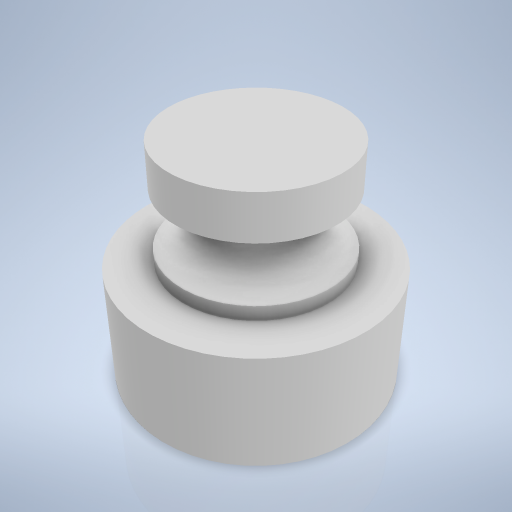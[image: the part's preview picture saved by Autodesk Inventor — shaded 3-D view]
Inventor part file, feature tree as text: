
AUTODESK INVENTOR PART (.ipt)
format: ipt  version: 2024.2 (Build 282272000, 272)  size: 270,336 bytes
history: native  units: mm
features: sketch x3, extrude x2, plane x1, revolve x1
ambient origin geometry x8: Origin, YZ Plane, XZ Plane, XY Plane, X Axis, Y Axis, Z Axis, Center Point
bodies: Volumenkörper1 (feature_tree)
feature tree (7):
  extrude  "Extrusion1"  Depth=20.0mm TaperAngle=0.0deg
  extrude  "Extrusion2"  Depth=20.0mm TaperAngle=0.0deg
  plane  "Arbeitsebene1"
  revolve  "Umdrehung1"
  sketch  "Skizze1"  dims[d0=45.0mm d1=20.0mm d2=0.0mm]
  sketch  "Skizze3"  dims[d3=30.0mm d4=20.0mm d5=0.0mm]
  sketch  "Skizze5"  dims[d6=0.0mm d8=20.0mm d10=7.5mm d11=360.0deg d13=5.0mm]
